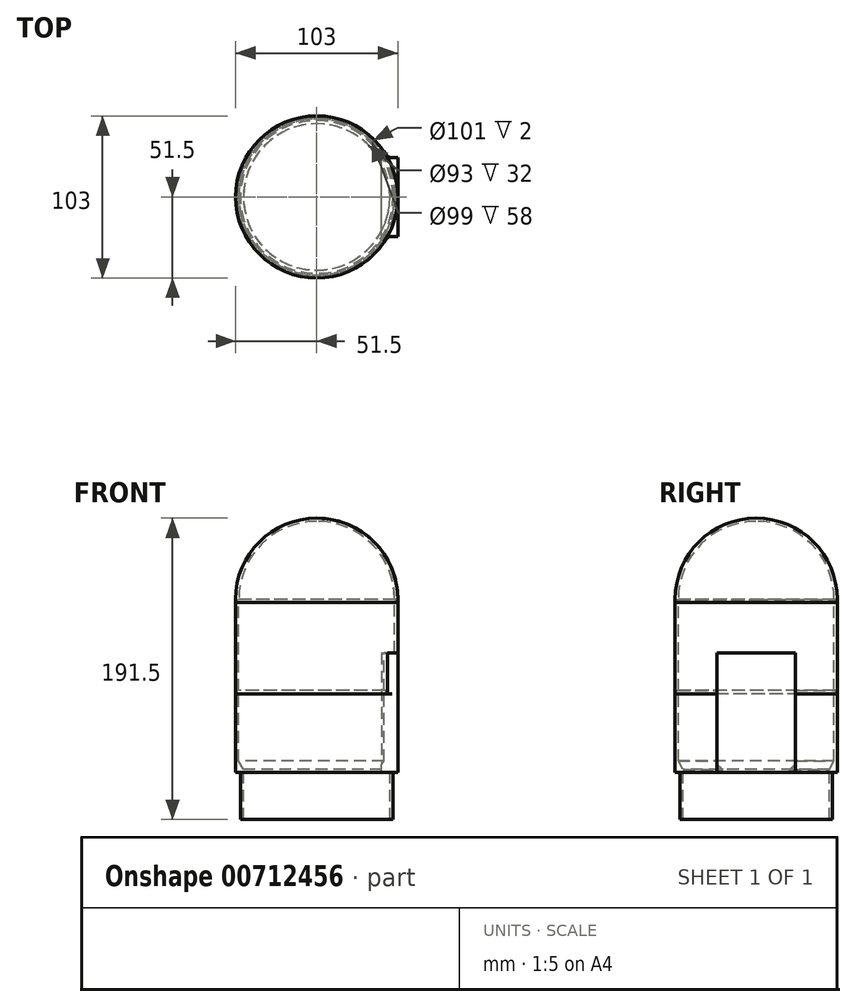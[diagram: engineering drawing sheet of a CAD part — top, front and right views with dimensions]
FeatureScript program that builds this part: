
annotation { "Feature Type Name" : "Feature", "Feature Type Description" : "" }
export const myFeature = defineFeature(function(context is Context, id is Id, definition is map)
    precondition{}
    {
        {
            var Q0;
            Q0=qCreatedBy(makeId("Front.planeOp"),FACE);
            var sketch = newSketch(context, id + "F0", { "sketchPlane" : qUnion([Q0])});
            skLineSegment(sketch, "E0", {"start": v(46.5, 0) * mm, "end": v(48.5, 0) * mm});
            skLineSegment(sketch, "E1", {"start": v(48.5, 0) * mm, "end": v(48.5, 30) * mm});
            skLineSegment(sketch, "E2", {"start": v(48.5, 30) * mm, "end": v(51.5, 30) * mm});
            skLineSegment(sketch, "E3", {"start": v(51.5, 30) * mm, "end": v(51.5, 80) * mm});
            skLineSegment(sketch, "E4", {"start": v(51.5, 80) * mm, "end": v(50.5, 80) * mm});
            skLineSegment(sketch, "E5", {"start": v(50.5, 80) * mm, "end": v(50.5, 82) * mm});
            skLineSegment(sketch, "E6", {"start": v(50.5, 82) * mm, "end": v(49.5, 82) * mm});
            skLineSegment(sketch, "E7", {"start": v(49.5, 82) * mm, "end": v(49.5, 37.2) * mm});
            skLineSegment(sketch, "E8", {"start": v(46.5, 32) * mm, "end": v(46.5, 0) * mm});
            skLineSegment(sketch, "E9", {"start": v(0, 177.79) * mm, "end": v(0, -43.37) * mm, "construction": true});
            skLineSegment(sketch, "E10", {"start": v(46.5, 32) * mm, "end": v(49.5, 37.2) * mm});
            skSolve(sketch);
        }
        {
            var Q0;
            Q0=makeQuery(id+"F0.imprint","IMPRINT",FACE,{"disambiguationData":[TD([[makeQuery(id+"F0.imprint","IMPRINT",EDGE,{"derivedFrom":sQuery(id+"F0.wireOp",EDGE,"E0")}),1.0]])]});
            var Q1;
            Q1=sQuery(id+"F0.wireOp",EDGE,"E9");
            revolve(context, id + "F1", {"surfaceOperationType" : NewSurfaceOperationType.NEW, "entities" : qUnion([Q0]), "axis" : qUnion([Q1]), "revolveType" : RevolveType.FULL});
        }
        {
            var Q0;
            Q0=qCreatedBy(makeId("Right.planeOp"),FACE);
            var Q1;
            Q1=sQuery(id+"F0.wireOp",VERTEX,"E2.end");
            cPlane(context, id + "F2", {"entities" : qUnion([Q0, Q1]), "cplaneType" : CPlaneType.PLANE_POINT, "offset" : 55 * mm, "width" : 150 * mm, "height" : 150 * mm});
        }
        {
            var Q0;
            Q0=qCreatedBy(id+"F2.planeOp",FACE);
            var sketch = newSketch(context, id + "F3", { "sketchPlane" : qUnion([Q0])});
            skLineSegment(sketch, "E11.bottom", {"start": v(-25, 106) * mm, "end": v(25, 106) * mm});
            skLineSegment(sketch, "E11.top", {"start": v(-25, 30) * mm, "end": v(25, 30) * mm});
            skLineSegment(sketch, "E11.left", {"start": v(-25, 106) * mm, "end": v(-25, 30) * mm});
            skLineSegment(sketch, "E11.right", {"start": v(25, 106) * mm, "end": v(25, 30) * mm});
            skSolve(sketch);
        }
        {
            var Q0;
            Q0 = qSketchRegion(id + "F3", true);
            extrude(context, id + "F4", {"entities" : qUnion([Q0]), "operationType" : NewBodyOperationType.ADD, "oppositeDirection" : true, "depth" : 10.2 * mm, "offsetDistance" : 25 * mm});
        }
        {
            var Q0;
            Q0=qCreatedBy(makeId("Front.planeOp"),FACE);
            var sketch = newSketch(context, id + "F5", { "sketchPlane" : qUnion([Q0])});
            skLineSegment(sketch, "E12", {"start": v(49.5, 82) * mm, "end": v(50.5, 82) * mm});
            skLineSegment(sketch, "E13", {"start": v(50.5, 82) * mm, "end": v(50.5, 80) * mm});
            skLineSegment(sketch, "E14", {"start": v(50.5, 80) * mm, "end": v(51.5, 80) * mm});
            skLineSegment(sketch, "E15", {"start": v(51.5, 80) * mm, "end": v(51.5, 140) * mm});
            skLineSegment(sketch, "E16", {"start": v(49.5, 140) * mm, "end": v(49.5, 82) * mm});
            skLineSegment(sketch, "E17", {"start": v(51.5, 140) * mm, "end": v(49.5, 140) * mm});
            skSolve(sketch);
        }
        {
            var Q0;
            Q0=makeQuery(id+"F5.imprint","IMPRINT",FACE,{"disambiguationData":[TD([[makeQuery(id+"F5.imprint","IMPRINT",EDGE,{"derivedFrom":sQuery(id+"F5.wireOp",EDGE,"E12")}),1.0]])]});
            var Q1;
            Q1=sQuery(id+"F0.wireOp",EDGE,"E9");
            revolve(context, id + "F6", {"surfaceOperationType" : NewSurfaceOperationType.NEW, "entities" : qUnion([Q0]), "axis" : qUnion([Q1]), "revolveType" : RevolveType.FULL});
        }
        {
            var Q0;
            Q0=qCreatedBy(makeId("Front.planeOp"),FACE);
            var sketch = newSketch(context, id + "F7", { "sketchPlane" : qUnion([Q0])});
            skLineSegment(sketch, "E18", {"start": v(51.5, 138) * mm, "end": v(50.5, 138) * mm});
            skLineSegment(sketch, "E19", {"start": v(51.5, 138) * mm, "end": v(51.5, 140) * mm});
            skLineSegment(sketch, "E20", {"start": v(50.5, 138) * mm, "end": v(50.5, 140) * mm});
            skLineSegment(sketch, "E21", {"start": v(50.5, 140) * mm, "end": v(49.5, 140) * mm});
            skArc(sketch, "E22", {"start": v(51.5, 140) * mm, "mid": v(36.42, 176.42) * mm, "end": v(0, 191.5) * mm});
            skArc(sketch, "E23", {"start": v(49.5, 140) * mm, "mid": v(35, 175) * mm, "end": v(0, 189.5) * mm});
            skLineSegment(sketch, "E24", {"start": v(0, 189.5) * mm, "end": v(0, 191.5) * mm});
            skSolve(sketch);
        }
        {
            var Q0;
            Q0=makeQuery(id+"F7.imprint","IMPRINT",FACE,{"disambiguationData":[TD([[makeQuery(id+"F7.imprint","IMPRINT",EDGE,{"derivedFrom":sQuery(id+"F7.wireOp",EDGE,"E18")}),-1.0]])]});
            var Q1;
            Q1=sQuery(id+"F0.wireOp",EDGE,"E9");
            revolve(context, id + "F8", {"surfaceOperationType" : NewSurfaceOperationType.NEW, "entities" : qUnion([Q0]), "axis" : qUnion([Q1]), "revolveType" : RevolveType.FULL});
        }
        {
            var Q0;
            Q0=makeQuery(id+"F8.opRevolve","SWEPT_BODY",BODY,{"disambiguationData":[OSD([sQuery(id+"F7.wireOp",EDGE,"E18"),sQuery(id+"F7.wireOp",EDGE,"E19"),sQuery(id+"F7.wireOp",EDGE,"E20"),sQuery(id+"F7.wireOp",EDGE,"E21"),sQuery(id+"F7.wireOp",EDGE,"E22"),sQuery(id+"F7.wireOp",EDGE,"E23"),sQuery(id+"F7.wireOp",EDGE,"E24")])]});
            var Q1;
            Q1=makeQuery(id+"F6.opRevolve","SWEPT_BODY",BODY,{"disambiguationData":[OSD([sQuery(id+"F5.wireOp",EDGE,"E12"),sQuery(id+"F5.wireOp",EDGE,"E13"),sQuery(id+"F5.wireOp",EDGE,"E14"),sQuery(id+"F5.wireOp",EDGE,"E15"),sQuery(id+"F5.wireOp",EDGE,"E16"),sQuery(id+"F5.wireOp",EDGE,"E17")])]});
            booleanBodies(context, id + "F9", {"operationType" : BooleanOperationType.SUBTRACTION, "tools" : qUnion([Q0]), "targets" : qUnion([Q1]), "keepTools" : true});
        }
        {
            var Q0;
            Q0=makeQuery(id+"F1.opRevolve","SWEPT_BODY",BODY,{"disambiguationData":[OSD([sQuery(id+"F0.wireOp",EDGE,"E0"),sQuery(id+"F0.wireOp",EDGE,"E1"),sQuery(id+"F0.wireOp",EDGE,"E2"),sQuery(id+"F0.wireOp",EDGE,"E3"),sQuery(id+"F0.wireOp",EDGE,"E4"),sQuery(id+"F0.wireOp",EDGE,"E5"),sQuery(id+"F0.wireOp",EDGE,"E6"),sQuery(id+"F0.wireOp",EDGE,"E7"),sQuery(id+"F0.wireOp",EDGE,"E8"),sQuery(id+"F0.wireOp",EDGE,"E10")])]});
            var Q1;
            Q1=makeQuery(id+"F6.opRevolve","SWEPT_BODY",BODY,{"disambiguationData":[OSD([sQuery(id+"F5.wireOp",EDGE,"E12"),sQuery(id+"F5.wireOp",EDGE,"E13"),sQuery(id+"F5.wireOp",EDGE,"E14"),sQuery(id+"F5.wireOp",EDGE,"E15"),sQuery(id+"F5.wireOp",EDGE,"E16"),sQuery(id+"F5.wireOp",EDGE,"E17")])]});
            booleanBodies(context, id + "F10", {"operationType" : BooleanOperationType.SUBTRACTION, "tools" : qUnion([Q0]), "targets" : qUnion([Q1]), "keepTools" : true});
        }
        {
            var Q0;
            Q0=makeQuery(id+"F4.boolean.opBoolean","INTERSECT",EDGE,{"derivedFrom":[makeQuery(id+"F1.opRevolve","SWEPT_FACE",FACE,{"disambiguationData":[OSD([sQuery(id+"F0.wireOp",EDGE,"E3")])]}),makeQuery(id+"F4.opExtrude","SWEPT_FACE",FACE,{"disambiguationData":[OSD([sQuery(id+"F3.wireOp",EDGE,"E11.left")])]})]});
            var Q1;
            Q1=makeQuery(id+"F4.boolean.opBoolean","INTERSECT",EDGE,{"derivedFrom":[makeQuery(id+"F1.opRevolve","SWEPT_FACE",FACE,{"disambiguationData":[OSD([sQuery(id+"F0.wireOp",EDGE,"E3")])]}),makeQuery(id+"F4.opExtrude","SWEPT_FACE",FACE,{"disambiguationData":[OSD([sQuery(id+"F3.wireOp",EDGE,"E11.right")])]})]});
            fillet(context, id + "F11", {"entities" : qUnion([Q0, Q1]), "radius" : 5 * mm, "tangentPropagation" : true, "allowEdgeOverflow" : false});
        }
    });
